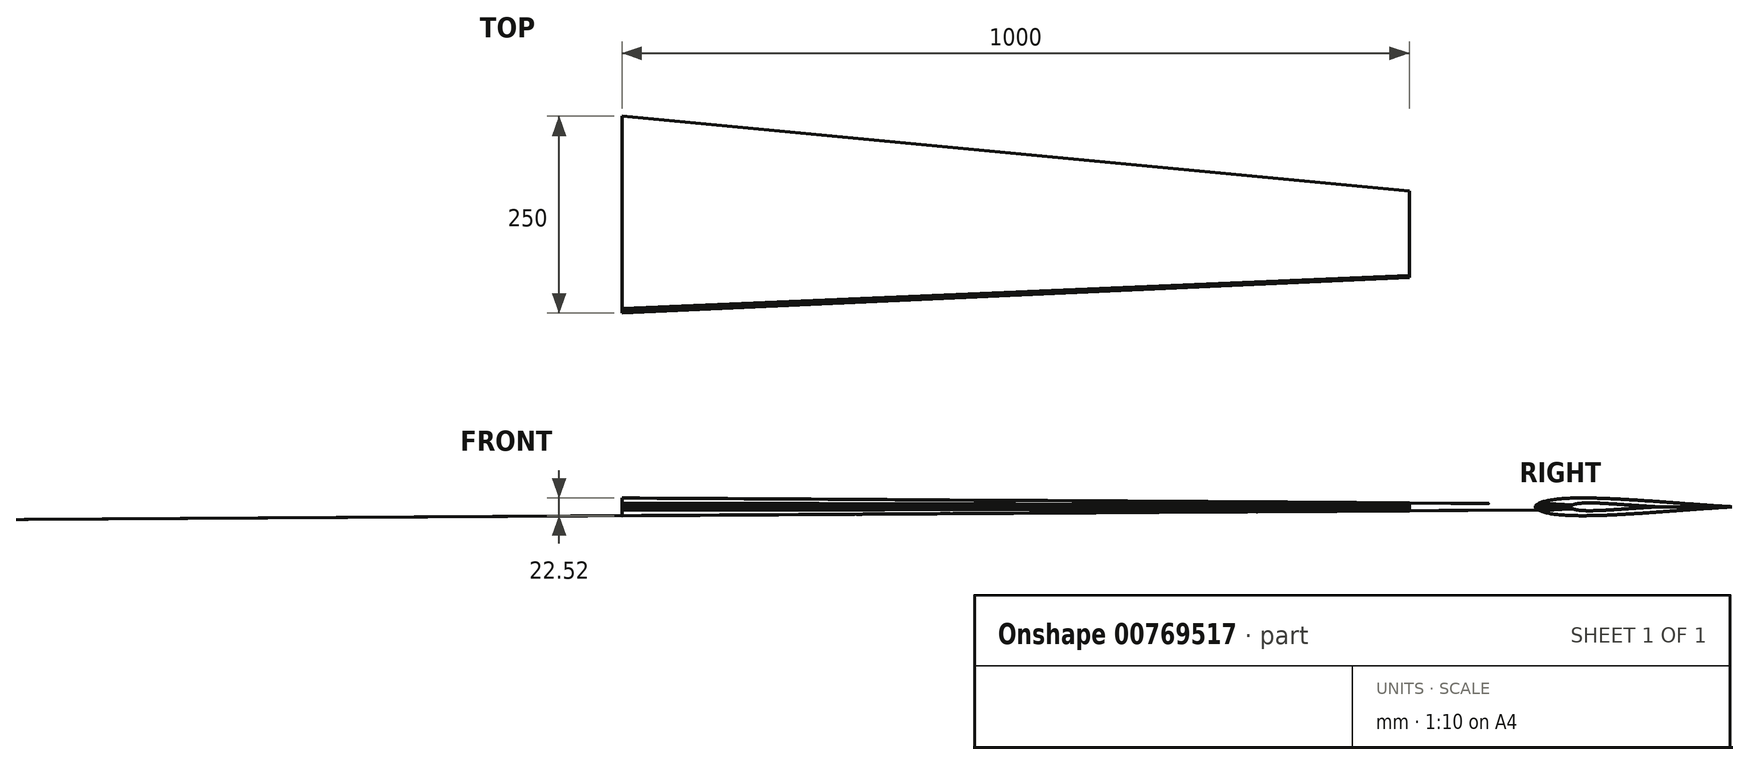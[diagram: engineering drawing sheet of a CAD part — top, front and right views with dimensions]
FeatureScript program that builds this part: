
annotation { "Feature Type Name" : "Feature", "Feature Type Description" : "" }
export const myFeature = defineFeature(function(context is Context, id is Id, definition is map)
    precondition{}
    {
        {
            var Q0;
            Q0=qCreatedBy(makeId("Right.planeOp"),FACE);
            var sketch = newSketch(context, id + "F0", { "sketchPlane" : qUnion([Q0])});
            skLineSegment(sketch, "E0", {"start": v(125, 0.07) * mm, "end": v(123.91, 0.12) * mm});
            skLineSegment(sketch, "E1", {"start": v(123.91, 0.12) * mm, "end": v(122.08, 0.22) * mm});
            skLineSegment(sketch, "E2", {"start": v(122.08, 0.22) * mm, "end": v(120.07, 0.34) * mm});
            skLineSegment(sketch, "E3", {"start": v(120.07, 0.34) * mm, "end": v(117.97, 0.48) * mm});
            skLineSegment(sketch, "E4", {"start": v(117.97, 0.48) * mm, "end": v(115.85, 0.61) * mm});
            skLineSegment(sketch, "E5", {"start": v(115.85, 0.61) * mm, "end": v(113.7, 0.75) * mm});
            skLineSegment(sketch, "E6", {"start": v(113.7, 0.75) * mm, "end": v(111.55, 0.89) * mm});
            skLineSegment(sketch, "E7", {"start": v(111.55, 0.89) * mm, "end": v(109.4, 1.02) * mm});
            skLineSegment(sketch, "E8", {"start": v(109.4, 1.02) * mm, "end": v(107.23, 1.16) * mm});
            skLineSegment(sketch, "E9", {"start": v(107.23, 1.16) * mm, "end": v(105.08, 1.3) * mm});
            skLineSegment(sketch, "E10", {"start": v(105.08, 1.3) * mm, "end": v(102.92, 1.44) * mm});
            skLineSegment(sketch, "E11", {"start": v(102.92, 1.44) * mm, "end": v(100.77, 1.58) * mm});
            skLineSegment(sketch, "E12", {"start": v(100.77, 1.58) * mm, "end": v(98.61, 1.72) * mm});
            skLineSegment(sketch, "E13", {"start": v(98.61, 1.72) * mm, "end": v(96.46, 1.87) * mm});
            skLineSegment(sketch, "E14", {"start": v(96.46, 1.87) * mm, "end": v(94.3, 2) * mm});
            skLineSegment(sketch, "E15", {"start": v(94.3, 2) * mm, "end": v(92.15, 2.16) * mm});
            skLineSegment(sketch, "E16", {"start": v(92.15, 2.16) * mm, "end": v(90, 2.3) * mm});
            skLineSegment(sketch, "E17", {"start": v(90, 2.3) * mm, "end": v(87.84, 2.46) * mm});
            skLineSegment(sketch, "E18", {"start": v(87.84, 2.46) * mm, "end": v(85.68, 2.6) * mm});
            skLineSegment(sketch, "E19", {"start": v(85.68, 2.6) * mm, "end": v(83.53, 2.76) * mm});
            skLineSegment(sketch, "E20", {"start": v(83.53, 2.76) * mm, "end": v(81.38, 2.91) * mm});
            skLineSegment(sketch, "E21", {"start": v(81.38, 2.91) * mm, "end": v(79.22, 3.06) * mm});
            skLineSegment(sketch, "E22", {"start": v(79.22, 3.06) * mm, "end": v(77.07, 3.22) * mm});
            skLineSegment(sketch, "E23", {"start": v(77.07, 3.22) * mm, "end": v(74.91, 3.38) * mm});
            skLineSegment(sketch, "E24", {"start": v(74.91, 3.38) * mm, "end": v(72.76, 3.53) * mm});
            skLineSegment(sketch, "E25", {"start": v(72.76, 3.53) * mm, "end": v(70.6, 3.69) * mm});
            skLineSegment(sketch, "E26", {"start": v(70.6, 3.69) * mm, "end": v(68.46, 3.85) * mm});
            skLineSegment(sketch, "E27", {"start": v(68.46, 3.85) * mm, "end": v(66.3, 4) * mm});
            skLineSegment(sketch, "E28", {"start": v(66.3, 4) * mm, "end": v(64.15, 4.16) * mm});
            skLineSegment(sketch, "E29", {"start": v(64.15, 4.16) * mm, "end": v(61.99, 4.32) * mm});
            skLineSegment(sketch, "E30", {"start": v(61.99, 4.32) * mm, "end": v(59.83, 4.48) * mm});
            skLineSegment(sketch, "E31", {"start": v(59.83, 4.48) * mm, "end": v(57.68, 4.64) * mm});
            skLineSegment(sketch, "E32", {"start": v(57.68, 4.64) * mm, "end": v(55.52, 4.8) * mm});
            skLineSegment(sketch, "E33", {"start": v(55.52, 4.8) * mm, "end": v(53.36, 4.96) * mm});
            skLineSegment(sketch, "E34", {"start": v(53.36, 4.96) * mm, "end": v(51.2, 5.12) * mm});
            skLineSegment(sketch, "E35", {"start": v(51.2, 5.12) * mm, "end": v(49.05, 5.28) * mm});
            skLineSegment(sketch, "E36", {"start": v(49.05, 5.28) * mm, "end": v(46.9, 5.44) * mm});
            skLineSegment(sketch, "E37", {"start": v(46.9, 5.44) * mm, "end": v(44.74, 5.6) * mm});
            skLineSegment(sketch, "E38", {"start": v(44.74, 5.6) * mm, "end": v(42.59, 5.76) * mm});
            skLineSegment(sketch, "E39", {"start": v(42.59, 5.76) * mm, "end": v(40.43, 5.92) * mm});
            skLineSegment(sketch, "E40", {"start": v(40.43, 5.92) * mm, "end": v(38.27, 6.08) * mm});
            skLineSegment(sketch, "E41", {"start": v(38.27, 6.08) * mm, "end": v(36.12, 6.24) * mm});
            skLineSegment(sketch, "E42", {"start": v(36.12, 6.24) * mm, "end": v(33.96, 6.4) * mm});
            skLineSegment(sketch, "E43", {"start": v(33.96, 6.4) * mm, "end": v(31.8, 6.56) * mm});
            skLineSegment(sketch, "E44", {"start": v(31.8, 6.56) * mm, "end": v(29.65, 6.71) * mm});
            skLineSegment(sketch, "E45", {"start": v(29.65, 6.71) * mm, "end": v(27.5, 6.87) * mm});
            skLineSegment(sketch, "E46", {"start": v(27.5, 6.87) * mm, "end": v(25.34, 7.03) * mm});
            skLineSegment(sketch, "E47", {"start": v(25.34, 7.03) * mm, "end": v(23.18, 7.18) * mm});
            skLineSegment(sketch, "E48", {"start": v(23.18, 7.18) * mm, "end": v(21.03, 7.33) * mm});
            skLineSegment(sketch, "E49", {"start": v(21.03, 7.33) * mm, "end": v(18.87, 7.49) * mm});
            skLineSegment(sketch, "E50", {"start": v(18.87, 7.49) * mm, "end": v(16.72, 7.64) * mm});
            skLineSegment(sketch, "E51", {"start": v(16.72, 7.64) * mm, "end": v(14.56, 7.79) * mm});
            skLineSegment(sketch, "E52", {"start": v(14.56, 7.79) * mm, "end": v(12.4, 7.94) * mm});
            skLineSegment(sketch, "E53", {"start": v(12.4, 7.94) * mm, "end": v(10.25, 8.08) * mm});
            skLineSegment(sketch, "E54", {"start": v(10.25, 8.08) * mm, "end": v(8.1, 8.23) * mm});
            skLineSegment(sketch, "E55", {"start": v(8.1, 8.23) * mm, "end": v(5.94, 8.37) * mm});
            skLineSegment(sketch, "E56", {"start": v(5.94, 8.37) * mm, "end": v(3.8, 8.51) * mm});
            skLineSegment(sketch, "E57", {"start": v(3.8, 8.51) * mm, "end": v(1.64, 8.65) * mm});
            skLineSegment(sketch, "E58", {"start": v(1.64, 8.65) * mm, "end": v(-0.52, 8.79) * mm});
            skLineSegment(sketch, "E59", {"start": v(-0.52, 8.79) * mm, "end": v(-2.67, 8.93) * mm});
            skLineSegment(sketch, "E60", {"start": v(-2.67, 8.93) * mm, "end": v(-4.82, 9.06) * mm});
            skLineSegment(sketch, "E61", {"start": v(-4.82, 9.06) * mm, "end": v(-6.98, 9.19) * mm});
            skLineSegment(sketch, "E62", {"start": v(-6.98, 9.19) * mm, "end": v(-9.13, 9.31) * mm});
            skLineSegment(sketch, "E63", {"start": v(-9.13, 9.31) * mm, "end": v(-11.29, 9.44) * mm});
            skLineSegment(sketch, "E64", {"start": v(-11.29, 9.44) * mm, "end": v(-13.44, 9.56) * mm});
            skLineSegment(sketch, "E65", {"start": v(-13.44, 9.56) * mm, "end": v(-15.6, 9.68) * mm});
            skLineSegment(sketch, "E66", {"start": v(-15.6, 9.68) * mm, "end": v(-17.75, 9.8) * mm});
            skLineSegment(sketch, "E67", {"start": v(-17.75, 9.8) * mm, "end": v(-19.9, 9.92) * mm});
            skLineSegment(sketch, "E68", {"start": v(-19.9, 9.92) * mm, "end": v(-22.05, 10.03) * mm});
            skLineSegment(sketch, "E69", {"start": v(-22.05, 10.03) * mm, "end": v(-24.2, 10.13) * mm});
            skLineSegment(sketch, "E70", {"start": v(-24.2, 10.13) * mm, "end": v(-26.35, 10.24) * mm});
            skLineSegment(sketch, "E71", {"start": v(-26.35, 10.24) * mm, "end": v(-28.5, 10.34) * mm});
            skLineSegment(sketch, "E72", {"start": v(-28.5, 10.34) * mm, "end": v(-30.66, 10.44) * mm});
            skLineSegment(sketch, "E73", {"start": v(-30.66, 10.44) * mm, "end": v(-32.8, 10.53) * mm});
            skLineSegment(sketch, "E74", {"start": v(-32.8, 10.53) * mm, "end": v(-34.96, 10.62) * mm});
            skLineSegment(sketch, "E75", {"start": v(-34.96, 10.62) * mm, "end": v(-37.1, 10.7) * mm});
            skLineSegment(sketch, "E76", {"start": v(-37.1, 10.7) * mm, "end": v(-39.26, 10.78) * mm});
            skLineSegment(sketch, "E77", {"start": v(-39.26, 10.78) * mm, "end": v(-41.4, 10.86) * mm});
            skLineSegment(sketch, "E78", {"start": v(-41.4, 10.86) * mm, "end": v(-43.55, 10.92) * mm});
            skLineSegment(sketch, "E79", {"start": v(-43.55, 10.92) * mm, "end": v(-45.7, 10.98) * mm});
            skLineSegment(sketch, "E80", {"start": v(-45.7, 10.98) * mm, "end": v(-47.85, 11.04) * mm});
            skLineSegment(sketch, "E81", {"start": v(-47.85, 11.04) * mm, "end": v(-50, 11.1) * mm});
            skLineSegment(sketch, "E82", {"start": v(-50, 11.1) * mm, "end": v(-52.14, 11.14) * mm});
            skLineSegment(sketch, "E83", {"start": v(-52.14, 11.14) * mm, "end": v(-54.29, 11.18) * mm});
            skLineSegment(sketch, "E84", {"start": v(-54.29, 11.18) * mm, "end": v(-56.43, 11.21) * mm});
            skLineSegment(sketch, "E85", {"start": v(-56.43, 11.21) * mm, "end": v(-58.57, 11.23) * mm});
            skLineSegment(sketch, "E86", {"start": v(-58.57, 11.23) * mm, "end": v(-60.71, 11.25) * mm});
            skLineSegment(sketch, "E87", {"start": v(-60.71, 11.25) * mm, "end": v(-62.86, 11.26) * mm});
            skLineSegment(sketch, "E88", {"start": v(-62.86, 11.26) * mm, "end": v(-65, 11.26) * mm});
            skLineSegment(sketch, "E89", {"start": v(-65, 11.26) * mm, "end": v(-67.14, 11.26) * mm});
            skLineSegment(sketch, "E90", {"start": v(-67.14, 11.26) * mm, "end": v(-69.27, 11.24) * mm});
            skLineSegment(sketch, "E91", {"start": v(-69.27, 11.24) * mm, "end": v(-71.4, 11.21) * mm});
            skLineSegment(sketch, "E92", {"start": v(-71.4, 11.21) * mm, "end": v(-73.54, 11.17) * mm});
            skLineSegment(sketch, "E93", {"start": v(-73.54, 11.17) * mm, "end": v(-75.67, 11.12) * mm});
            skLineSegment(sketch, "E94", {"start": v(-75.67, 11.12) * mm, "end": v(-77.8, 11.06) * mm});
            skLineSegment(sketch, "E95", {"start": v(-77.8, 11.06) * mm, "end": v(-79.93, 11) * mm});
            skLineSegment(sketch, "E96", {"start": v(-79.93, 11) * mm, "end": v(-82.05, 10.9) * mm});
            skLineSegment(sketch, "E97", {"start": v(-82.05, 10.9) * mm, "end": v(-84.17, 10.8) * mm});
            skLineSegment(sketch, "E98", {"start": v(-84.17, 10.8) * mm, "end": v(-86.29, 10.7) * mm});
            skLineSegment(sketch, "E99", {"start": v(-86.29, 10.7) * mm, "end": v(-88.4, 10.56) * mm});
            skLineSegment(sketch, "E100", {"start": v(-88.4, 10.56) * mm, "end": v(-90.5, 10.4) * mm});
            skLineSegment(sketch, "E101", {"start": v(-90.5, 10.4) * mm, "end": v(-92.6, 10.24) * mm});
            skLineSegment(sketch, "E102", {"start": v(-92.6, 10.24) * mm, "end": v(-94.7, 10.05) * mm});
            skLineSegment(sketch, "E103", {"start": v(-94.7, 10.05) * mm, "end": v(-96.78, 9.85) * mm});
            skLineSegment(sketch, "E104", {"start": v(-96.78, 9.85) * mm, "end": v(-98.86, 9.61) * mm});
            skLineSegment(sketch, "E105", {"start": v(-98.86, 9.61) * mm, "end": v(-100.93, 9.36) * mm});
            skLineSegment(sketch, "E106", {"start": v(-100.93, 9.36) * mm, "end": v(-102.98, 9.07) * mm});
            skLineSegment(sketch, "E107", {"start": v(-102.98, 9.07) * mm, "end": v(-105.02, 8.75) * mm});
            skLineSegment(sketch, "E108", {"start": v(-105.02, 8.75) * mm, "end": v(-107.03, 8.4) * mm});
            skLineSegment(sketch, "E109", {"start": v(-107.03, 8.4) * mm, "end": v(-109.02, 8.02) * mm});
            skLineSegment(sketch, "E110", {"start": v(-109.02, 8.02) * mm, "end": v(-110.97, 7.6) * mm});
            skLineSegment(sketch, "E111", {"start": v(-110.97, 7.6) * mm, "end": v(-112.88, 7.12) * mm});
            skLineSegment(sketch, "E112", {"start": v(-112.88, 7.12) * mm, "end": v(-114.72, 6.6) * mm});
            skLineSegment(sketch, "E113", {"start": v(-114.72, 6.6) * mm, "end": v(-116.46, 6.05) * mm});
            skLineSegment(sketch, "E114", {"start": v(-116.46, 6.05) * mm, "end": v(-118.05, 5.47) * mm});
            skLineSegment(sketch, "E115", {"start": v(-118.05, 5.47) * mm, "end": v(-119.45, 4.88) * mm});
            skLineSegment(sketch, "E116", {"start": v(-119.45, 4.88) * mm, "end": v(-120.64, 4.31) * mm});
            skLineSegment(sketch, "E117", {"start": v(-120.64, 4.31) * mm, "end": v(-121.6, 3.79) * mm});
            skLineSegment(sketch, "E118", {"start": v(-121.6, 3.79) * mm, "end": v(-122.37, 3.3) * mm});
            skLineSegment(sketch, "E119", {"start": v(-122.37, 3.3) * mm, "end": v(-122.98, 2.87) * mm});
            skLineSegment(sketch, "E120", {"start": v(-122.98, 2.87) * mm, "end": v(-123.47, 2.47) * mm});
            skLineSegment(sketch, "E121", {"start": v(-123.47, 2.47) * mm, "end": v(-123.86, 2.1) * mm});
            skLineSegment(sketch, "E122", {"start": v(-123.86, 2.1) * mm, "end": v(-124.18, 1.78) * mm});
            skLineSegment(sketch, "E123", {"start": v(-124.18, 1.78) * mm, "end": v(-124.44, 1.47) * mm});
            skLineSegment(sketch, "E124", {"start": v(-124.44, 1.47) * mm, "end": v(-124.64, 1.17) * mm});
            skLineSegment(sketch, "E125", {"start": v(-124.64, 1.17) * mm, "end": v(-124.78, 0.88) * mm});
            skLineSegment(sketch, "E126", {"start": v(-124.78, 0.88) * mm, "end": v(-124.88, 0.6) * mm});
            skLineSegment(sketch, "E127", {"start": v(-124.88, 0.61) * mm, "end": v(-124.95, 0.35) * mm});
            skLineSegment(sketch, "E128", {"start": v(-124.95, 0.35) * mm, "end": v(-125, 0.12) * mm});
            skLineSegment(sketch, "E129", {"start": v(-125, 0.12) * mm, "end": v(-125, -0.12) * mm});
            skLineSegment(sketch, "E130", {"start": v(-125, -0.12) * mm, "end": v(-124.95, -0.35) * mm});
            skLineSegment(sketch, "E131", {"start": v(-124.95, -0.35) * mm, "end": v(-124.88, -0.61) * mm});
            skLineSegment(sketch, "E132", {"start": v(-124.88, -0.61) * mm, "end": v(-124.78, -0.89) * mm});
            skLineSegment(sketch, "E133", {"start": v(-124.78, -0.89) * mm, "end": v(-124.64, -1.17) * mm});
            skLineSegment(sketch, "E134", {"start": v(-124.64, -1.17) * mm, "end": v(-124.44, -1.47) * mm});
            skLineSegment(sketch, "E135", {"start": v(-124.44, -1.47) * mm, "end": v(-124.18, -1.78) * mm});
            skLineSegment(sketch, "E136", {"start": v(-124.18, -1.78) * mm, "end": v(-123.86, -2.1) * mm});
            skLineSegment(sketch, "E137", {"start": v(-123.86, -2.1) * mm, "end": v(-123.47, -2.47) * mm});
            skLineSegment(sketch, "E138", {"start": v(-123.47, -2.47) * mm, "end": v(-122.98, -2.87) * mm});
            skLineSegment(sketch, "E139", {"start": v(-122.98, -2.87) * mm, "end": v(-122.37, -3.3) * mm});
            skLineSegment(sketch, "E140", {"start": v(-122.37, -3.3) * mm, "end": v(-121.6, -3.79) * mm});
            skLineSegment(sketch, "E141", {"start": v(-121.6, -3.79) * mm, "end": v(-120.64, -4.31) * mm});
            skLineSegment(sketch, "E142", {"start": v(-120.64, -4.31) * mm, "end": v(-119.45, -4.88) * mm});
            skLineSegment(sketch, "E143", {"start": v(-119.45, -4.88) * mm, "end": v(-118.05, -5.47) * mm});
            skLineSegment(sketch, "E144", {"start": v(-118.05, -5.47) * mm, "end": v(-116.46, -6.05) * mm});
            skLineSegment(sketch, "E145", {"start": v(-116.46, -6.05) * mm, "end": v(-114.72, -6.6) * mm});
            skLineSegment(sketch, "E146", {"start": v(-114.72, -6.6) * mm, "end": v(-112.88, -7.12) * mm});
            skLineSegment(sketch, "E147", {"start": v(-112.88, -7.12) * mm, "end": v(-110.97, -7.6) * mm});
            skLineSegment(sketch, "E148", {"start": v(-110.97, -7.6) * mm, "end": v(-109.02, -8.02) * mm});
            skLineSegment(sketch, "E149", {"start": v(-109.02, -8.02) * mm, "end": v(-107.03, -8.4) * mm});
            skLineSegment(sketch, "E150", {"start": v(-107.03, -8.4) * mm, "end": v(-105.02, -8.75) * mm});
            skLineSegment(sketch, "E151", {"start": v(-105.02, -8.75) * mm, "end": v(-102.98, -9.07) * mm});
            skLineSegment(sketch, "E152", {"start": v(-102.98, -9.07) * mm, "end": v(-100.93, -9.36) * mm});
            skLineSegment(sketch, "E153", {"start": v(-100.93, -9.36) * mm, "end": v(-98.86, -9.61) * mm});
            skLineSegment(sketch, "E154", {"start": v(-98.86, -9.61) * mm, "end": v(-96.78, -9.85) * mm});
            skLineSegment(sketch, "E155", {"start": v(-96.78, -9.85) * mm, "end": v(-94.7, -10.05) * mm});
            skLineSegment(sketch, "E156", {"start": v(-94.7, -10.05) * mm, "end": v(-92.6, -10.24) * mm});
            skLineSegment(sketch, "E157", {"start": v(-92.6, -10.24) * mm, "end": v(-90.5, -10.4) * mm});
            skLineSegment(sketch, "E158", {"start": v(-90.5, -10.4) * mm, "end": v(-88.4, -10.56) * mm});
            skLineSegment(sketch, "E159", {"start": v(-88.4, -10.56) * mm, "end": v(-86.29, -10.7) * mm});
            skLineSegment(sketch, "E160", {"start": v(-86.29, -10.7) * mm, "end": v(-84.17, -10.8) * mm});
            skLineSegment(sketch, "E161", {"start": v(-84.17, -10.8) * mm, "end": v(-82.05, -10.9) * mm});
            skLineSegment(sketch, "E162", {"start": v(-82.05, -10.9) * mm, "end": v(-79.93, -11) * mm});
            skLineSegment(sketch, "E163", {"start": v(-79.93, -11) * mm, "end": v(-77.8, -11.06) * mm});
            skLineSegment(sketch, "E164", {"start": v(-77.8, -11.06) * mm, "end": v(-75.67, -11.12) * mm});
            skLineSegment(sketch, "E165", {"start": v(-75.67, -11.12) * mm, "end": v(-73.54, -11.17) * mm});
            skLineSegment(sketch, "E166", {"start": v(-73.54, -11.17) * mm, "end": v(-71.4, -11.21) * mm});
            skLineSegment(sketch, "E167", {"start": v(-71.4, -11.21) * mm, "end": v(-69.27, -11.24) * mm});
            skLineSegment(sketch, "E168", {"start": v(-69.27, -11.24) * mm, "end": v(-67.14, -11.26) * mm});
            skLineSegment(sketch, "E169", {"start": v(-67.14, -11.26) * mm, "end": v(-65, -11.26) * mm});
            skLineSegment(sketch, "E170", {"start": v(-65, -11.26) * mm, "end": v(-62.86, -11.26) * mm});
            skLineSegment(sketch, "E171", {"start": v(-62.86, -11.26) * mm, "end": v(-60.71, -11.25) * mm});
            skLineSegment(sketch, "E172", {"start": v(-60.71, -11.25) * mm, "end": v(-58.57, -11.23) * mm});
            skLineSegment(sketch, "E173", {"start": v(-58.57, -11.23) * mm, "end": v(-56.43, -11.21) * mm});
            skLineSegment(sketch, "E174", {"start": v(-56.43, -11.21) * mm, "end": v(-54.28, -11.18) * mm});
            skLineSegment(sketch, "E175", {"start": v(-54.28, -11.18) * mm, "end": v(-52.14, -11.14) * mm});
            skLineSegment(sketch, "E176", {"start": v(-52.14, -11.14) * mm, "end": v(-50, -11.1) * mm});
            skLineSegment(sketch, "E177", {"start": v(-50, -11.1) * mm, "end": v(-47.85, -11.04) * mm});
            skLineSegment(sketch, "E178", {"start": v(-47.85, -11.04) * mm, "end": v(-45.7, -10.98) * mm});
            skLineSegment(sketch, "E179", {"start": v(-45.7, -10.98) * mm, "end": v(-43.55, -10.92) * mm});
            skLineSegment(sketch, "E180", {"start": v(-43.55, -10.92) * mm, "end": v(-41.4, -10.86) * mm});
            skLineSegment(sketch, "E181", {"start": v(-41.4, -10.86) * mm, "end": v(-39.26, -10.78) * mm});
            skLineSegment(sketch, "E182", {"start": v(-39.26, -10.78) * mm, "end": v(-37.1, -10.7) * mm});
            skLineSegment(sketch, "E183", {"start": v(-37.1, -10.7) * mm, "end": v(-34.96, -10.62) * mm});
            skLineSegment(sketch, "E184", {"start": v(-34.96, -10.62) * mm, "end": v(-32.8, -10.53) * mm});
            skLineSegment(sketch, "E185", {"start": v(-32.8, -10.53) * mm, "end": v(-30.66, -10.44) * mm});
            skLineSegment(sketch, "E186", {"start": v(-30.66, -10.44) * mm, "end": v(-28.5, -10.34) * mm});
            skLineSegment(sketch, "E187", {"start": v(-28.5, -10.34) * mm, "end": v(-26.35, -10.24) * mm});
            skLineSegment(sketch, "E188", {"start": v(-26.35, -10.24) * mm, "end": v(-24.2, -10.13) * mm});
            skLineSegment(sketch, "E189", {"start": v(-24.2, -10.13) * mm, "end": v(-22.05, -10.03) * mm});
            skLineSegment(sketch, "E190", {"start": v(-22.05, -10.03) * mm, "end": v(-19.9, -9.92) * mm});
            skLineSegment(sketch, "E191", {"start": v(-19.9, -9.92) * mm, "end": v(-17.74, -9.8) * mm});
            skLineSegment(sketch, "E192", {"start": v(-17.74, -9.8) * mm, "end": v(-15.6, -9.68) * mm});
            skLineSegment(sketch, "E193", {"start": v(-15.6, -9.68) * mm, "end": v(-13.44, -9.56) * mm});
            skLineSegment(sketch, "E194", {"start": v(-13.44, -9.56) * mm, "end": v(-11.28, -9.44) * mm});
            skLineSegment(sketch, "E195", {"start": v(-11.28, -9.44) * mm, "end": v(-9.13, -9.31) * mm});
            skLineSegment(sketch, "E196", {"start": v(-9.13, -9.31) * mm, "end": v(-6.98, -9.19) * mm});
            skLineSegment(sketch, "E197", {"start": v(-6.98, -9.19) * mm, "end": v(-4.82, -9.05) * mm});
            skLineSegment(sketch, "E198", {"start": v(-4.82, -9.05) * mm, "end": v(-2.67, -8.92) * mm});
            skLineSegment(sketch, "E199", {"start": v(-2.67, -8.92) * mm, "end": v(-0.52, -8.79) * mm});
            skLineSegment(sketch, "E200", {"start": v(-0.52, -8.79) * mm, "end": v(1.64, -8.65) * mm});
            skLineSegment(sketch, "E201", {"start": v(1.64, -8.65) * mm, "end": v(3.8, -8.51) * mm});
            skLineSegment(sketch, "E202", {"start": v(3.8, -8.51) * mm, "end": v(5.95, -8.37) * mm});
            skLineSegment(sketch, "E203", {"start": v(5.95, -8.37) * mm, "end": v(8.1, -8.23) * mm});
            skLineSegment(sketch, "E204", {"start": v(8.1, -8.23) * mm, "end": v(10.25, -8.08) * mm});
            skLineSegment(sketch, "E205", {"start": v(10.25, -8.08) * mm, "end": v(12.4, -7.94) * mm});
            skLineSegment(sketch, "E206", {"start": v(12.4, -7.94) * mm, "end": v(14.56, -7.79) * mm});
            skLineSegment(sketch, "E207", {"start": v(14.56, -7.79) * mm, "end": v(16.72, -7.64) * mm});
            skLineSegment(sketch, "E208", {"start": v(16.72, -7.64) * mm, "end": v(18.87, -7.49) * mm});
            skLineSegment(sketch, "E209", {"start": v(18.87, -7.49) * mm, "end": v(21.03, -7.33) * mm});
            skLineSegment(sketch, "E210", {"start": v(21.03, -7.33) * mm, "end": v(23.18, -7.18) * mm});
            skLineSegment(sketch, "E211", {"start": v(23.18, -7.18) * mm, "end": v(25.34, -7.03) * mm});
            skLineSegment(sketch, "E212", {"start": v(25.34, -7.03) * mm, "end": v(27.5, -6.87) * mm});
            skLineSegment(sketch, "E213", {"start": v(27.5, -6.87) * mm, "end": v(29.65, -6.71) * mm});
            skLineSegment(sketch, "E214", {"start": v(29.65, -6.71) * mm, "end": v(31.8, -6.56) * mm});
            skLineSegment(sketch, "E215", {"start": v(31.8, -6.56) * mm, "end": v(33.96, -6.4) * mm});
            skLineSegment(sketch, "E216", {"start": v(33.96, -6.4) * mm, "end": v(36.1, -6.24) * mm});
            skLineSegment(sketch, "E217", {"start": v(36.1, -6.24) * mm, "end": v(38.26, -6.08) * mm});
            skLineSegment(sketch, "E218", {"start": v(38.26, -6.08) * mm, "end": v(40.42, -5.92) * mm});
            skLineSegment(sketch, "E219", {"start": v(40.42, -5.92) * mm, "end": v(42.57, -5.76) * mm});
            skLineSegment(sketch, "E220", {"start": v(42.57, -5.76) * mm, "end": v(44.73, -5.6) * mm});
            skLineSegment(sketch, "E221", {"start": v(44.73, -5.6) * mm, "end": v(46.88, -5.44) * mm});
            skLineSegment(sketch, "E222", {"start": v(46.88, -5.44) * mm, "end": v(49.03, -5.28) * mm});
            skLineSegment(sketch, "E223", {"start": v(49.03, -5.28) * mm, "end": v(51.19, -5.12) * mm});
            skLineSegment(sketch, "E224", {"start": v(51.19, -5.12) * mm, "end": v(53.34, -4.96) * mm});
            skLineSegment(sketch, "E225", {"start": v(53.34, -4.96) * mm, "end": v(55.5, -4.8) * mm});
            skLineSegment(sketch, "E226", {"start": v(55.5, -4.8) * mm, "end": v(57.66, -4.64) * mm});
            skLineSegment(sketch, "E227", {"start": v(57.66, -4.64) * mm, "end": v(59.81, -4.48) * mm});
            skLineSegment(sketch, "E228", {"start": v(59.81, -4.48) * mm, "end": v(61.97, -4.32) * mm});
            skLineSegment(sketch, "E229", {"start": v(61.97, -4.32) * mm, "end": v(64.13, -4.16) * mm});
            skLineSegment(sketch, "E230", {"start": v(64.13, -4.16) * mm, "end": v(66.28, -4) * mm});
            skLineSegment(sketch, "E231", {"start": v(66.28, -4) * mm, "end": v(68.44, -3.85) * mm});
            skLineSegment(sketch, "E232", {"start": v(68.44, -3.85) * mm, "end": v(70.6, -3.69) * mm});
            skLineSegment(sketch, "E233", {"start": v(70.6, -3.69) * mm, "end": v(72.75, -3.53) * mm});
            skLineSegment(sketch, "E234", {"start": v(72.75, -3.53) * mm, "end": v(74.9, -3.38) * mm});
            skLineSegment(sketch, "E235", {"start": v(74.9, -3.38) * mm, "end": v(77.06, -3.22) * mm});
            skLineSegment(sketch, "E236", {"start": v(77.06, -3.22) * mm, "end": v(79.22, -3.06) * mm});
            skLineSegment(sketch, "E237", {"start": v(79.22, -3.06) * mm, "end": v(81.37, -2.91) * mm});
            skLineSegment(sketch, "E238", {"start": v(81.37, -2.91) * mm, "end": v(83.53, -2.76) * mm});
            skLineSegment(sketch, "E239", {"start": v(83.53, -2.76) * mm, "end": v(85.68, -2.6) * mm});
            skLineSegment(sketch, "E240", {"start": v(85.68, -2.6) * mm, "end": v(87.84, -2.46) * mm});
            skLineSegment(sketch, "E241", {"start": v(87.84, -2.46) * mm, "end": v(90, -2.3) * mm});
            skLineSegment(sketch, "E242", {"start": v(90, -2.3) * mm, "end": v(92.15, -2.16) * mm});
            skLineSegment(sketch, "E243", {"start": v(92.15, -2.16) * mm, "end": v(94.3, -2) * mm});
            skLineSegment(sketch, "E244", {"start": v(94.3, -2) * mm, "end": v(96.46, -1.87) * mm});
            skLineSegment(sketch, "E245", {"start": v(96.46, -1.87) * mm, "end": v(98.61, -1.72) * mm});
            skLineSegment(sketch, "E246", {"start": v(98.61, -1.72) * mm, "end": v(100.77, -1.58) * mm});
            skLineSegment(sketch, "E247", {"start": v(100.77, -1.58) * mm, "end": v(102.92, -1.44) * mm});
            skLineSegment(sketch, "E248", {"start": v(102.92, -1.44) * mm, "end": v(105.08, -1.3) * mm});
            skLineSegment(sketch, "E249", {"start": v(105.08, -1.3) * mm, "end": v(107.24, -1.16) * mm});
            skLineSegment(sketch, "E250", {"start": v(107.24, -1.16) * mm, "end": v(109.4, -1.02) * mm});
            skLineSegment(sketch, "E251", {"start": v(109.4, -1.02) * mm, "end": v(111.55, -0.89) * mm});
            skLineSegment(sketch, "E252", {"start": v(111.55, -0.89) * mm, "end": v(113.7, -0.75) * mm});
            skLineSegment(sketch, "E253", {"start": v(113.7, -0.75) * mm, "end": v(115.85, -0.61) * mm});
            skLineSegment(sketch, "E254", {"start": v(115.85, -0.61) * mm, "end": v(117.98, -0.48) * mm});
            skLineSegment(sketch, "E255", {"start": v(117.98, -0.48) * mm, "end": v(120.07, -0.34) * mm});
            skLineSegment(sketch, "E256", {"start": v(120.07, -0.34) * mm, "end": v(122.08, -0.22) * mm});
            skLineSegment(sketch, "E257", {"start": v(122.08, -0.22) * mm, "end": v(123.91, -0.12) * mm});
            skLineSegment(sketch, "E258", {"start": v(123.91, -0.12) * mm, "end": v(125, -0.07) * mm});
            skLineSegment(sketch, "E259", {"start": v(125, -0.07) * mm, "end": v(125, 0.07) * mm});
            skSolve(sketch);
        }
        {
            var Q0;
            Q0=qCreatedBy(makeId("Right.planeOp"),FACE);
            cPlane(context, id + "F1", {"entities" : qUnion([Q0]), "cplaneType" : CPlaneType.OFFSET, "offset" : 1000 * mm, "width" : 150 * mm, "height" : 150 * mm});
        }
        {
            var Q0;
            Q0=qCreatedBy(id+"F1.planeOp",FACE);
            var sketch = newSketch(context, id + "F2", { "sketchPlane" : qUnion([Q0])});
            skLineSegment(sketch, "E260", {"start": v(30, 0.06) * mm, "end": v(29.5, 0.08) * mm});
            skLineSegment(sketch, "E261", {"start": v(29.5, 0.08) * mm, "end": v(28.65, 0.13) * mm});
            skLineSegment(sketch, "E262", {"start": v(28.65, 0.13) * mm, "end": v(27.74, 0.17) * mm});
            skLineSegment(sketch, "E263", {"start": v(27.74, 0.17) * mm, "end": v(26.81, 0.22) * mm});
            skLineSegment(sketch, "E264", {"start": v(26.81, 0.22) * mm, "end": v(25.88, 0.27) * mm});
            skLineSegment(sketch, "E265", {"start": v(25.88, 0.27) * mm, "end": v(24.94, 0.32) * mm});
            skLineSegment(sketch, "E266", {"start": v(24.94, 0.32) * mm, "end": v(24, 0.37) * mm});
            skLineSegment(sketch, "E267", {"start": v(24, 0.37) * mm, "end": v(23.07, 0.42) * mm});
            skLineSegment(sketch, "E268", {"start": v(23.07, 0.42) * mm, "end": v(22.13, 0.47) * mm});
            skLineSegment(sketch, "E269", {"start": v(22.13, 0.47) * mm, "end": v(21.2, 0.53) * mm});
            skLineSegment(sketch, "E270", {"start": v(21.2, 0.53) * mm, "end": v(20.25, 0.58) * mm});
            skLineSegment(sketch, "E271", {"start": v(20.25, 0.58) * mm, "end": v(19.31, 0.63) * mm});
            skLineSegment(sketch, "E272", {"start": v(19.31, 0.63) * mm, "end": v(18.37, 0.69) * mm});
            skLineSegment(sketch, "E273", {"start": v(18.37, 0.69) * mm, "end": v(17.44, 0.75) * mm});
            skLineSegment(sketch, "E274", {"start": v(17.44, 0.75) * mm, "end": v(16.5, 0.8) * mm});
            skLineSegment(sketch, "E275", {"start": v(16.5, 0.8) * mm, "end": v(15.56, 0.86) * mm});
            skLineSegment(sketch, "E276", {"start": v(15.56, 0.86) * mm, "end": v(14.62, 0.92) * mm});
            skLineSegment(sketch, "E277", {"start": v(14.62, 0.92) * mm, "end": v(13.69, 0.98) * mm});
            skLineSegment(sketch, "E278", {"start": v(13.69, 0.98) * mm, "end": v(12.75, 1.04) * mm});
            skLineSegment(sketch, "E279", {"start": v(12.75, 1.04) * mm, "end": v(11.82, 1.1) * mm});
            skLineSegment(sketch, "E280", {"start": v(11.82, 1.1) * mm, "end": v(10.88, 1.16) * mm});
            skLineSegment(sketch, "E281", {"start": v(10.88, 1.16) * mm, "end": v(9.95, 1.22) * mm});
            skLineSegment(sketch, "E282", {"start": v(9.95, 1.22) * mm, "end": v(9, 1.28) * mm});
            skLineSegment(sketch, "E283", {"start": v(9, 1.28) * mm, "end": v(8.07, 1.34) * mm});
            skLineSegment(sketch, "E284", {"start": v(8.07, 1.34) * mm, "end": v(7.13, 1.4) * mm});
            skLineSegment(sketch, "E285", {"start": v(7.13, 1.4) * mm, "end": v(6.2, 1.46) * mm});
            skLineSegment(sketch, "E286", {"start": v(6.2, 1.46) * mm, "end": v(5.26, 1.53) * mm});
            skLineSegment(sketch, "E287", {"start": v(5.26, 1.53) * mm, "end": v(4.33, 1.59) * mm});
            skLineSegment(sketch, "E288", {"start": v(4.33, 1.59) * mm, "end": v(3.39, 1.65) * mm});
            skLineSegment(sketch, "E289", {"start": v(3.39, 1.65) * mm, "end": v(2.45, 1.71) * mm});
            skLineSegment(sketch, "E290", {"start": v(2.45, 1.71) * mm, "end": v(1.51, 1.78) * mm});
            skLineSegment(sketch, "E291", {"start": v(1.51, 1.78) * mm, "end": v(0.58, 1.84) * mm});
            skLineSegment(sketch, "E292", {"start": v(0.58, 1.84) * mm, "end": v(-0.35, 1.9) * mm});
            skLineSegment(sketch, "E293", {"start": v(-0.35, 1.9) * mm, "end": v(-1.3, 1.97) * mm});
            skLineSegment(sketch, "E294", {"start": v(-1.3, 1.97) * mm, "end": v(-2.23, 2.04) * mm});
            skLineSegment(sketch, "E295", {"start": v(-2.23, 2.04) * mm, "end": v(-3.16, 2.1) * mm});
            skLineSegment(sketch, "E296", {"start": v(-3.16, 2.1) * mm, "end": v(-4.1, 2.16) * mm});
            skLineSegment(sketch, "E297", {"start": v(-4.1, 2.16) * mm, "end": v(-5.03, 2.23) * mm});
            skLineSegment(sketch, "E298", {"start": v(-5.03, 2.23) * mm, "end": v(-5.96, 2.3) * mm});
            skLineSegment(sketch, "E299", {"start": v(-5.96, 2.3) * mm, "end": v(-6.9, 2.36) * mm});
            skLineSegment(sketch, "E300", {"start": v(-6.9, 2.36) * mm, "end": v(-7.84, 2.43) * mm});
            skLineSegment(sketch, "E301", {"start": v(-7.84, 2.43) * mm, "end": v(-8.78, 2.5) * mm});
            skLineSegment(sketch, "E302", {"start": v(-8.78, 2.5) * mm, "end": v(-9.72, 2.56) * mm});
            skLineSegment(sketch, "E303", {"start": v(-9.72, 2.56) * mm, "end": v(-10.65, 2.62) * mm});
            skLineSegment(sketch, "E304", {"start": v(-10.65, 2.62) * mm, "end": v(-11.6, 2.69) * mm});
            skLineSegment(sketch, "E305", {"start": v(-11.6, 2.69) * mm, "end": v(-12.53, 2.76) * mm});
            skLineSegment(sketch, "E306", {"start": v(-12.53, 2.76) * mm, "end": v(-13.47, 2.82) * mm});
            skLineSegment(sketch, "E307", {"start": v(-13.47, 2.82) * mm, "end": v(-14.41, 2.89) * mm});
            skLineSegment(sketch, "E308", {"start": v(-14.41, 2.89) * mm, "end": v(-15.35, 2.95) * mm});
            skLineSegment(sketch, "E309", {"start": v(-15.35, 2.95) * mm, "end": v(-16.29, 3.02) * mm});
            skLineSegment(sketch, "E310", {"start": v(-16.29, 3.02) * mm, "end": v(-17.22, 3.08) * mm});
            skLineSegment(sketch, "E311", {"start": v(-17.22, 3.08) * mm, "end": v(-18.16, 3.15) * mm});
            skLineSegment(sketch, "E312", {"start": v(-18.16, 3.15) * mm, "end": v(-19.1, 3.21) * mm});
            skLineSegment(sketch, "E313", {"start": v(-19.1, 3.21) * mm, "end": v(-20.03, 3.28) * mm});
            skLineSegment(sketch, "E314", {"start": v(-20.03, 3.28) * mm, "end": v(-20.97, 3.34) * mm});
            skLineSegment(sketch, "E315", {"start": v(-20.97, 3.34) * mm, "end": v(-21.9, 3.4) * mm});
            skLineSegment(sketch, "E316", {"start": v(-21.9, 3.4) * mm, "end": v(-22.84, 3.46) * mm});
            skLineSegment(sketch, "E317", {"start": v(-22.84, 3.46) * mm, "end": v(-23.77, 3.53) * mm});
            skLineSegment(sketch, "E318", {"start": v(-23.77, 3.53) * mm, "end": v(-24.7, 3.59) * mm});
            skLineSegment(sketch, "E319", {"start": v(-24.7, 3.59) * mm, "end": v(-25.64, 3.65) * mm});
            skLineSegment(sketch, "E320", {"start": v(-25.64, 3.65) * mm, "end": v(-26.58, 3.71) * mm});
            skLineSegment(sketch, "E321", {"start": v(-26.58, 3.71) * mm, "end": v(-27.52, 3.77) * mm});
            skLineSegment(sketch, "E322", {"start": v(-27.52, 3.77) * mm, "end": v(-28.45, 3.83) * mm});
            skLineSegment(sketch, "E323", {"start": v(-28.45, 3.83) * mm, "end": v(-29.4, 3.89) * mm});
            skLineSegment(sketch, "E324", {"start": v(-29.4, 3.89) * mm, "end": v(-30.33, 3.94) * mm});
            skLineSegment(sketch, "E325", {"start": v(-30.33, 3.94) * mm, "end": v(-31.26, 4) * mm});
            skLineSegment(sketch, "E326", {"start": v(-31.26, 4) * mm, "end": v(-32.2, 4.06) * mm});
            skLineSegment(sketch, "E327", {"start": v(-32.2, 4.06) * mm, "end": v(-33.13, 4.11) * mm});
            skLineSegment(sketch, "E328", {"start": v(-33.13, 4.11) * mm, "end": v(-34.07, 4.17) * mm});
            skLineSegment(sketch, "E329", {"start": v(-34.07, 4.17) * mm, "end": v(-35, 4.22) * mm});
            skLineSegment(sketch, "E330", {"start": v(-35, 4.22) * mm, "end": v(-35.95, 4.27) * mm});
            skLineSegment(sketch, "E331", {"start": v(-35.95, 4.27) * mm, "end": v(-36.88, 4.33) * mm});
            skLineSegment(sketch, "E332", {"start": v(-36.88, 4.33) * mm, "end": v(-37.82, 4.37) * mm});
            skLineSegment(sketch, "E333", {"start": v(-37.82, 4.37) * mm, "end": v(-38.75, 4.42) * mm});
            skLineSegment(sketch, "E334", {"start": v(-38.75, 4.42) * mm, "end": v(-39.7, 4.47) * mm});
            skLineSegment(sketch, "E335", {"start": v(-39.7, 4.47) * mm, "end": v(-40.63, 4.52) * mm});
            skLineSegment(sketch, "E336", {"start": v(-40.63, 4.52) * mm, "end": v(-41.57, 4.56) * mm});
            skLineSegment(sketch, "E337", {"start": v(-41.57, 4.56) * mm, "end": v(-42.5, 4.6) * mm});
            skLineSegment(sketch, "E338", {"start": v(-42.5, 4.6) * mm, "end": v(-43.44, 4.64) * mm});
            skLineSegment(sketch, "E339", {"start": v(-43.44, 4.64) * mm, "end": v(-44.38, 4.68) * mm});
            skLineSegment(sketch, "E340", {"start": v(-44.38, 4.68) * mm, "end": v(-45.31, 4.72) * mm});
            skLineSegment(sketch, "E341", {"start": v(-45.31, 4.72) * mm, "end": v(-46.25, 4.75) * mm});
            skLineSegment(sketch, "E342", {"start": v(-46.25, 4.75) * mm, "end": v(-47.19, 4.78) * mm});
            skLineSegment(sketch, "E343", {"start": v(-47.19, 4.78) * mm, "end": v(-48.12, 4.81) * mm});
            skLineSegment(sketch, "E344", {"start": v(-48.12, 4.81) * mm, "end": v(-49.06, 4.84) * mm});
            skLineSegment(sketch, "E345", {"start": v(-49.06, 4.84) * mm, "end": v(-50, 4.87) * mm});
            skLineSegment(sketch, "E346", {"start": v(-50, 4.87) * mm, "end": v(-50.93, 4.89) * mm});
            skLineSegment(sketch, "E347", {"start": v(-50.93, 4.89) * mm, "end": v(-51.87, 4.9) * mm});
            skLineSegment(sketch, "E348", {"start": v(-51.87, 4.9) * mm, "end": v(-52.8, 4.92) * mm});
            skLineSegment(sketch, "E349", {"start": v(-52.8, 4.92) * mm, "end": v(-53.74, 4.93) * mm});
            skLineSegment(sketch, "E350", {"start": v(-53.74, 4.93) * mm, "end": v(-54.67, 4.94) * mm});
            skLineSegment(sketch, "E351", {"start": v(-54.67, 4.94) * mm, "end": v(-55.6, 4.95) * mm});
            skLineSegment(sketch, "E352", {"start": v(-55.6, 4.95) * mm, "end": v(-56.54, 4.95) * mm});
            skLineSegment(sketch, "E353", {"start": v(-56.54, 4.95) * mm, "end": v(-57.47, 4.95) * mm});
            skLineSegment(sketch, "E354", {"start": v(-57.47, 4.95) * mm, "end": v(-58.4, 4.94) * mm});
            skLineSegment(sketch, "E355", {"start": v(-58.4, 4.94) * mm, "end": v(-59.34, 4.93) * mm});
            skLineSegment(sketch, "E356", {"start": v(-59.34, 4.93) * mm, "end": v(-60.27, 4.91) * mm});
            skLineSegment(sketch, "E357", {"start": v(-60.27, 4.91) * mm, "end": v(-61.2, 4.89) * mm});
            skLineSegment(sketch, "E358", {"start": v(-61.2, 4.89) * mm, "end": v(-62.13, 4.86) * mm});
            skLineSegment(sketch, "E359", {"start": v(-62.13, 4.86) * mm, "end": v(-63.06, 4.82) * mm});
            skLineSegment(sketch, "E360", {"start": v(-63.06, 4.82) * mm, "end": v(-63.98, 4.78) * mm});
            skLineSegment(sketch, "E361", {"start": v(-63.98, 4.78) * mm, "end": v(-64.9, 4.73) * mm});
            skLineSegment(sketch, "E362", {"start": v(-64.9, 4.73) * mm, "end": v(-65.83, 4.67) * mm});
            skLineSegment(sketch, "E363", {"start": v(-65.83, 4.67) * mm, "end": v(-66.75, 4.6) * mm});
            skLineSegment(sketch, "E364", {"start": v(-66.75, 4.6) * mm, "end": v(-67.67, 4.53) * mm});
            skLineSegment(sketch, "E365", {"start": v(-67.67, 4.53) * mm, "end": v(-68.58, 4.44) * mm});
            skLineSegment(sketch, "E366", {"start": v(-68.58, 4.44) * mm, "end": v(-69.5, 4.34) * mm});
            skLineSegment(sketch, "E367", {"start": v(-69.5, 4.34) * mm, "end": v(-70.4, 4.23) * mm});
            skLineSegment(sketch, "E368", {"start": v(-70.4, 4.23) * mm, "end": v(-71.3, 4.1) * mm});
            skLineSegment(sketch, "E369", {"start": v(-71.3, 4.1) * mm, "end": v(-72.19, 3.95) * mm});
            skLineSegment(sketch, "E370", {"start": v(-72.19, 3.95) * mm, "end": v(-73.06, 3.79) * mm});
            skLineSegment(sketch, "E371", {"start": v(-73.06, 3.79) * mm, "end": v(-73.93, 3.6) * mm});
            skLineSegment(sketch, "E372", {"start": v(-73.93, 3.6) * mm, "end": v(-74.78, 3.39) * mm});
            skLineSegment(sketch, "E373", {"start": v(-74.78, 3.39) * mm, "end": v(-75.6, 3.15) * mm});
            skLineSegment(sketch, "E374", {"start": v(-75.6, 3.15) * mm, "end": v(-76.39, 2.88) * mm});
            skLineSegment(sketch, "E375", {"start": v(-76.39, 2.88) * mm, "end": v(-77.12, 2.6) * mm});
            skLineSegment(sketch, "E376", {"start": v(-77.12, 2.6) * mm, "end": v(-77.76, 2.3) * mm});
            skLineSegment(sketch, "E377", {"start": v(-77.76, 2.3) * mm, "end": v(-78.3, 2) * mm});
            skLineSegment(sketch, "E378", {"start": v(-78.3, 2) * mm, "end": v(-78.74, 1.71) * mm});
            skLineSegment(sketch, "E379", {"start": v(-78.74, 1.71) * mm, "end": v(-79.08, 1.46) * mm});
            skLineSegment(sketch, "E380", {"start": v(-79.08, 1.46) * mm, "end": v(-79.33, 1.24) * mm});
            skLineSegment(sketch, "E381", {"start": v(-79.33, 1.24) * mm, "end": v(-79.53, 1.04) * mm});
            skLineSegment(sketch, "E382", {"start": v(-79.53, 1.04) * mm, "end": v(-79.67, 0.86) * mm});
            skLineSegment(sketch, "E383", {"start": v(-79.67, 0.86) * mm, "end": v(-79.8, 0.7) * mm});
            skLineSegment(sketch, "E384", {"start": v(-79.8, 0.7) * mm, "end": v(-79.87, 0.55) * mm});
            skLineSegment(sketch, "E385", {"start": v(-79.87, 0.55) * mm, "end": v(-79.92, 0.41) * mm});
            skLineSegment(sketch, "E386", {"start": v(-79.92, 0.41) * mm, "end": v(-79.95, 0.28) * mm});
            skLineSegment(sketch, "E387", {"start": v(-79.95, 0.28) * mm, "end": v(-79.97, 0.17) * mm});
            skLineSegment(sketch, "E388", {"start": v(-79.97, 0.17) * mm, "end": v(-80, 0.06) * mm});
            skLineSegment(sketch, "E389", {"start": v(-80, 0.06) * mm, "end": v(-80, -0.04) * mm});
            skLineSegment(sketch, "E390", {"start": v(-80, -0.04) * mm, "end": v(-79.98, -0.15) * mm});
            skLineSegment(sketch, "E391", {"start": v(-79.98, -0.15) * mm, "end": v(-79.95, -0.27) * mm});
            skLineSegment(sketch, "E392", {"start": v(-79.95, -0.27) * mm, "end": v(-79.92, -0.4) * mm});
            skLineSegment(sketch, "E393", {"start": v(-79.92, -0.4) * mm, "end": v(-79.88, -0.54) * mm});
            skLineSegment(sketch, "E394", {"start": v(-79.88, -0.54) * mm, "end": v(-79.8, -0.7) * mm});
            skLineSegment(sketch, "E395", {"start": v(-79.8, -0.7) * mm, "end": v(-79.68, -0.85) * mm});
            skLineSegment(sketch, "E396", {"start": v(-79.68, -0.85) * mm, "end": v(-79.53, -1.04) * mm});
            skLineSegment(sketch, "E397", {"start": v(-79.53, -1.04) * mm, "end": v(-79.34, -1.24) * mm});
            skLineSegment(sketch, "E398", {"start": v(-79.34, -1.24) * mm, "end": v(-79.08, -1.46) * mm});
            skLineSegment(sketch, "E399", {"start": v(-79.08, -1.46) * mm, "end": v(-78.74, -1.72) * mm});
            skLineSegment(sketch, "E400", {"start": v(-78.74, -1.72) * mm, "end": v(-78.3, -2) * mm});
            skLineSegment(sketch, "E401", {"start": v(-78.3, -2) * mm, "end": v(-77.75, -2.3) * mm});
            skLineSegment(sketch, "E402", {"start": v(-77.75, -2.3) * mm, "end": v(-77.1, -2.6) * mm});
            skLineSegment(sketch, "E403", {"start": v(-77.1, -2.6) * mm, "end": v(-76.36, -2.9) * mm});
            skLineSegment(sketch, "E404", {"start": v(-76.36, -2.9) * mm, "end": v(-75.58, -3.15) * mm});
            skLineSegment(sketch, "E405", {"start": v(-75.58, -3.15) * mm, "end": v(-74.75, -3.4) * mm});
            skLineSegment(sketch, "E406", {"start": v(-74.75, -3.4) * mm, "end": v(-73.9, -3.6) * mm});
            skLineSegment(sketch, "E407", {"start": v(-73.9, -3.6) * mm, "end": v(-73.04, -3.8) * mm});
            skLineSegment(sketch, "E408", {"start": v(-73.04, -3.8) * mm, "end": v(-72.16, -3.96) * mm});
            skLineSegment(sketch, "E409", {"start": v(-72.16, -3.96) * mm, "end": v(-71.27, -4.1) * mm});
            skLineSegment(sketch, "E410", {"start": v(-71.27, -4.1) * mm, "end": v(-70.37, -4.23) * mm});
            skLineSegment(sketch, "E411", {"start": v(-70.37, -4.23) * mm, "end": v(-69.47, -4.34) * mm});
            skLineSegment(sketch, "E412", {"start": v(-69.47, -4.34) * mm, "end": v(-68.56, -4.44) * mm});
            skLineSegment(sketch, "E413", {"start": v(-68.56, -4.44) * mm, "end": v(-67.64, -4.53) * mm});
            skLineSegment(sketch, "E414", {"start": v(-67.64, -4.53) * mm, "end": v(-66.73, -4.6) * mm});
            skLineSegment(sketch, "E415", {"start": v(-66.73, -4.6) * mm, "end": v(-65.8, -4.67) * mm});
            skLineSegment(sketch, "E416", {"start": v(-65.8, -4.67) * mm, "end": v(-64.88, -4.73) * mm});
            skLineSegment(sketch, "E417", {"start": v(-64.88, -4.73) * mm, "end": v(-63.96, -4.78) * mm});
            skLineSegment(sketch, "E418", {"start": v(-63.96, -4.78) * mm, "end": v(-63.03, -4.82) * mm});
            skLineSegment(sketch, "E419", {"start": v(-63.03, -4.82) * mm, "end": v(-62.1, -4.86) * mm});
            skLineSegment(sketch, "E420", {"start": v(-62.1, -4.86) * mm, "end": v(-61.17, -4.89) * mm});
            skLineSegment(sketch, "E421", {"start": v(-61.17, -4.89) * mm, "end": v(-60.24, -4.91) * mm});
            skLineSegment(sketch, "E422", {"start": v(-60.24, -4.91) * mm, "end": v(-59.31, -4.93) * mm});
            skLineSegment(sketch, "E423", {"start": v(-59.31, -4.93) * mm, "end": v(-58.38, -4.94) * mm});
            skLineSegment(sketch, "E424", {"start": v(-58.38, -4.94) * mm, "end": v(-57.45, -4.95) * mm});
            skLineSegment(sketch, "E425", {"start": v(-57.45, -4.95) * mm, "end": v(-56.51, -4.95) * mm});
            skLineSegment(sketch, "E426", {"start": v(-56.51, -4.95) * mm, "end": v(-55.58, -4.95) * mm});
            skLineSegment(sketch, "E427", {"start": v(-55.58, -4.95) * mm, "end": v(-54.65, -4.94) * mm});
            skLineSegment(sketch, "E428", {"start": v(-54.65, -4.94) * mm, "end": v(-53.71, -4.93) * mm});
            skLineSegment(sketch, "E429", {"start": v(-53.71, -4.93) * mm, "end": v(-52.78, -4.92) * mm});
            skLineSegment(sketch, "E430", {"start": v(-52.78, -4.92) * mm, "end": v(-51.84, -4.9) * mm});
            skLineSegment(sketch, "E431", {"start": v(-51.84, -4.9) * mm, "end": v(-50.9, -4.89) * mm});
            skLineSegment(sketch, "E432", {"start": v(-50.9, -4.89) * mm, "end": v(-49.97, -4.87) * mm});
            skLineSegment(sketch, "E433", {"start": v(-49.97, -4.87) * mm, "end": v(-49.03, -4.84) * mm});
            skLineSegment(sketch, "E434", {"start": v(-49.03, -4.84) * mm, "end": v(-48.1, -4.81) * mm});
            skLineSegment(sketch, "E435", {"start": v(-48.1, -4.81) * mm, "end": v(-47.16, -4.78) * mm});
            skLineSegment(sketch, "E436", {"start": v(-47.16, -4.78) * mm, "end": v(-46.22, -4.75) * mm});
            skLineSegment(sketch, "E437", {"start": v(-46.22, -4.75) * mm, "end": v(-45.3, -4.72) * mm});
            skLineSegment(sketch, "E438", {"start": v(-45.3, -4.72) * mm, "end": v(-44.35, -4.68) * mm});
            skLineSegment(sketch, "E439", {"start": v(-44.35, -4.68) * mm, "end": v(-43.42, -4.64) * mm});
            skLineSegment(sketch, "E440", {"start": v(-43.42, -4.64) * mm, "end": v(-42.48, -4.6) * mm});
            skLineSegment(sketch, "E441", {"start": v(-42.48, -4.6) * mm, "end": v(-41.55, -4.56) * mm});
            skLineSegment(sketch, "E442", {"start": v(-41.55, -4.56) * mm, "end": v(-40.61, -4.51) * mm});
            skLineSegment(sketch, "E443", {"start": v(-40.61, -4.51) * mm, "end": v(-39.68, -4.47) * mm});
            skLineSegment(sketch, "E444", {"start": v(-39.68, -4.47) * mm, "end": v(-38.74, -4.42) * mm});
            skLineSegment(sketch, "E445", {"start": v(-38.74, -4.42) * mm, "end": v(-37.8, -4.37) * mm});
            skLineSegment(sketch, "E446", {"start": v(-37.8, -4.37) * mm, "end": v(-36.86, -4.32) * mm});
            skLineSegment(sketch, "E447", {"start": v(-36.86, -4.32) * mm, "end": v(-35.93, -4.27) * mm});
            skLineSegment(sketch, "E448", {"start": v(-35.93, -4.27) * mm, "end": v(-34.99, -4.22) * mm});
            skLineSegment(sketch, "E449", {"start": v(-34.99, -4.22) * mm, "end": v(-34.05, -4.17) * mm});
            skLineSegment(sketch, "E450", {"start": v(-34.05, -4.17) * mm, "end": v(-33.11, -4.11) * mm});
            skLineSegment(sketch, "E451", {"start": v(-33.11, -4.11) * mm, "end": v(-32.18, -4.06) * mm});
            skLineSegment(sketch, "E452", {"start": v(-32.18, -4.06) * mm, "end": v(-31.24, -4) * mm});
            skLineSegment(sketch, "E453", {"start": v(-31.24, -4) * mm, "end": v(-30.3, -3.94) * mm});
            skLineSegment(sketch, "E454", {"start": v(-30.3, -3.94) * mm, "end": v(-29.36, -3.89) * mm});
            skLineSegment(sketch, "E455", {"start": v(-29.36, -3.89) * mm, "end": v(-28.43, -3.83) * mm});
            skLineSegment(sketch, "E456", {"start": v(-28.43, -3.83) * mm, "end": v(-27.5, -3.77) * mm});
            skLineSegment(sketch, "E457", {"start": v(-27.5, -3.77) * mm, "end": v(-26.56, -3.7) * mm});
            skLineSegment(sketch, "E458", {"start": v(-26.56, -3.7) * mm, "end": v(-25.62, -3.65) * mm});
            skLineSegment(sketch, "E459", {"start": v(-25.62, -3.65) * mm, "end": v(-24.7, -3.59) * mm});
            skLineSegment(sketch, "E460", {"start": v(-24.7, -3.59) * mm, "end": v(-23.75, -3.53) * mm});
            skLineSegment(sketch, "E461", {"start": v(-23.75, -3.53) * mm, "end": v(-22.82, -3.46) * mm});
            skLineSegment(sketch, "E462", {"start": v(-22.82, -3.46) * mm, "end": v(-21.88, -3.4) * mm});
            skLineSegment(sketch, "E463", {"start": v(-21.88, -3.4) * mm, "end": v(-20.95, -3.34) * mm});
            skLineSegment(sketch, "E464", {"start": v(-20.95, -3.34) * mm, "end": v(-20.01, -3.27) * mm});
            skLineSegment(sketch, "E465", {"start": v(-20.01, -3.27) * mm, "end": v(-19.08, -3.2) * mm});
            skLineSegment(sketch, "E466", {"start": v(-19.08, -3.2) * mm, "end": v(-18.14, -3.14) * mm});
            skLineSegment(sketch, "E467", {"start": v(-18.14, -3.14) * mm, "end": v(-17.2, -3.08) * mm});
            skLineSegment(sketch, "E468", {"start": v(-17.2, -3.08) * mm, "end": v(-16.26, -3.02) * mm});
            skLineSegment(sketch, "E469", {"start": v(-16.26, -3.02) * mm, "end": v(-15.32, -2.95) * mm});
            skLineSegment(sketch, "E470", {"start": v(-15.32, -2.95) * mm, "end": v(-14.38, -2.89) * mm});
            skLineSegment(sketch, "E471", {"start": v(-14.38, -2.89) * mm, "end": v(-13.45, -2.82) * mm});
            skLineSegment(sketch, "E472", {"start": v(-13.45, -2.82) * mm, "end": v(-12.5, -2.75) * mm});
            skLineSegment(sketch, "E473", {"start": v(-12.5, -2.75) * mm, "end": v(-11.57, -2.69) * mm});
            skLineSegment(sketch, "E474", {"start": v(-11.57, -2.69) * mm, "end": v(-10.63, -2.62) * mm});
            skLineSegment(sketch, "E475", {"start": v(-10.63, -2.62) * mm, "end": v(-9.7, -2.56) * mm});
            skLineSegment(sketch, "E476", {"start": v(-9.7, -2.56) * mm, "end": v(-8.76, -2.49) * mm});
            skLineSegment(sketch, "E477", {"start": v(-8.76, -2.49) * mm, "end": v(-7.82, -2.42) * mm});
            skLineSegment(sketch, "E478", {"start": v(-7.82, -2.42) * mm, "end": v(-6.88, -2.36) * mm});
            skLineSegment(sketch, "E479", {"start": v(-6.88, -2.36) * mm, "end": v(-5.94, -2.3) * mm});
            skLineSegment(sketch, "E480", {"start": v(-5.94, -2.3) * mm, "end": v(-5, -2.23) * mm});
            skLineSegment(sketch, "E481", {"start": v(-5, -2.23) * mm, "end": v(-4.07, -2.16) * mm});
            skLineSegment(sketch, "E482", {"start": v(-4.07, -2.16) * mm, "end": v(-3.13, -2.1) * mm});
            skLineSegment(sketch, "E483", {"start": v(-3.13, -2.1) * mm, "end": v(-2.2, -2.03) * mm});
            skLineSegment(sketch, "E484", {"start": v(-2.2, -2.03) * mm, "end": v(-1.26, -1.97) * mm});
            skLineSegment(sketch, "E485", {"start": v(-1.26, -1.97) * mm, "end": v(-0.33, -1.9) * mm});
            skLineSegment(sketch, "E486", {"start": v(-0.33, -1.9) * mm, "end": v(0.6, -1.84) * mm});
            skLineSegment(sketch, "E487", {"start": v(0.6, -1.84) * mm, "end": v(1.54, -1.78) * mm});
            skLineSegment(sketch, "E488", {"start": v(1.54, -1.78) * mm, "end": v(2.48, -1.71) * mm});
            skLineSegment(sketch, "E489", {"start": v(2.48, -1.71) * mm, "end": v(3.41, -1.65) * mm});
            skLineSegment(sketch, "E490", {"start": v(3.41, -1.65) * mm, "end": v(4.35, -1.59) * mm});
            skLineSegment(sketch, "E491", {"start": v(4.35, -1.59) * mm, "end": v(5.28, -1.52) * mm});
            skLineSegment(sketch, "E492", {"start": v(5.28, -1.52) * mm, "end": v(6.2, -1.46) * mm});
            skLineSegment(sketch, "E493", {"start": v(6.2, -1.46) * mm, "end": v(7.14, -1.4) * mm});
            skLineSegment(sketch, "E494", {"start": v(7.14, -1.4) * mm, "end": v(8.07, -1.34) * mm});
            skLineSegment(sketch, "E495", {"start": v(8.07, -1.34) * mm, "end": v(9, -1.28) * mm});
            skLineSegment(sketch, "E496", {"start": v(9, -1.28) * mm, "end": v(9.93, -1.22) * mm});
            skLineSegment(sketch, "E497", {"start": v(9.93, -1.22) * mm, "end": v(10.87, -1.16) * mm});
            skLineSegment(sketch, "E498", {"start": v(10.87, -1.16) * mm, "end": v(11.8, -1.1) * mm});
            skLineSegment(sketch, "E499", {"start": v(11.8, -1.1) * mm, "end": v(12.74, -1.04) * mm});
            skLineSegment(sketch, "E500", {"start": v(12.74, -1.04) * mm, "end": v(13.68, -0.98) * mm});
            skLineSegment(sketch, "E501", {"start": v(13.68, -0.98) * mm, "end": v(14.62, -0.92) * mm});
            skLineSegment(sketch, "E502", {"start": v(14.62, -0.92) * mm, "end": v(15.56, -0.86) * mm});
            skLineSegment(sketch, "E503", {"start": v(15.56, -0.86) * mm, "end": v(16.5, -0.8) * mm});
            skLineSegment(sketch, "E504", {"start": v(16.5, -0.8) * mm, "end": v(17.44, -0.75) * mm});
            skLineSegment(sketch, "E505", {"start": v(17.44, -0.75) * mm, "end": v(18.37, -0.69) * mm});
            skLineSegment(sketch, "E506", {"start": v(18.37, -0.69) * mm, "end": v(19.31, -0.63) * mm});
            skLineSegment(sketch, "E507", {"start": v(19.31, -0.63) * mm, "end": v(20.25, -0.58) * mm});
            skLineSegment(sketch, "E508", {"start": v(20.25, -0.58) * mm, "end": v(21.2, -0.53) * mm});
            skLineSegment(sketch, "E509", {"start": v(21.2, -0.53) * mm, "end": v(22.13, -0.47) * mm});
            skLineSegment(sketch, "E510", {"start": v(22.13, -0.47) * mm, "end": v(23.07, -0.42) * mm});
            skLineSegment(sketch, "E511", {"start": v(23.07, -0.42) * mm, "end": v(24, -0.37) * mm});
            skLineSegment(sketch, "E512", {"start": v(24, -0.37) * mm, "end": v(24.94, -0.32) * mm});
            skLineSegment(sketch, "E513", {"start": v(24.94, -0.32) * mm, "end": v(25.88, -0.27) * mm});
            skLineSegment(sketch, "E514", {"start": v(25.88, -0.27) * mm, "end": v(26.81, -0.22) * mm});
            skLineSegment(sketch, "E515", {"start": v(26.81, -0.22) * mm, "end": v(27.74, -0.17) * mm});
            skLineSegment(sketch, "E516", {"start": v(27.74, -0.17) * mm, "end": v(28.65, -0.13) * mm});
            skLineSegment(sketch, "E517", {"start": v(28.65, -0.13) * mm, "end": v(29.5, -0.08) * mm});
            skLineSegment(sketch, "E518", {"start": v(29.5, -0.08) * mm, "end": v(30, -0.06) * mm});
            skLineSegment(sketch, "E519", {"start": v(30, 0.06) * mm, "end": v(30, -0.06) * mm});
            skSolve(sketch);
        }
        {
            var Q0;
            Q0=makeQuery(id+"F0.imprint","IMPRINT",FACE,{"disambiguationData":[TD([[makeQuery(id+"F0.imprint","IMPRINT",EDGE,{"derivedFrom":sQuery(id+"F0.wireOp",EDGE,"E0")}),1.0]])]});
            var Q1;
            Q1=makeQuery(id+"F2.imprint","IMPRINT",FACE,{"disambiguationData":[TD([[makeQuery(id+"F2.imprint","IMPRINT",EDGE,{"derivedFrom":sQuery(id+"F2.wireOp",EDGE,"E260")}),1.0]])]});
            loft(context, id + "F3", {"sheetProfilesArray" : [{ "sheetProfileEntities" : qUnion([Q0]) }, { "sheetProfileEntities" : qUnion([Q1]) }]});
        }
    });
